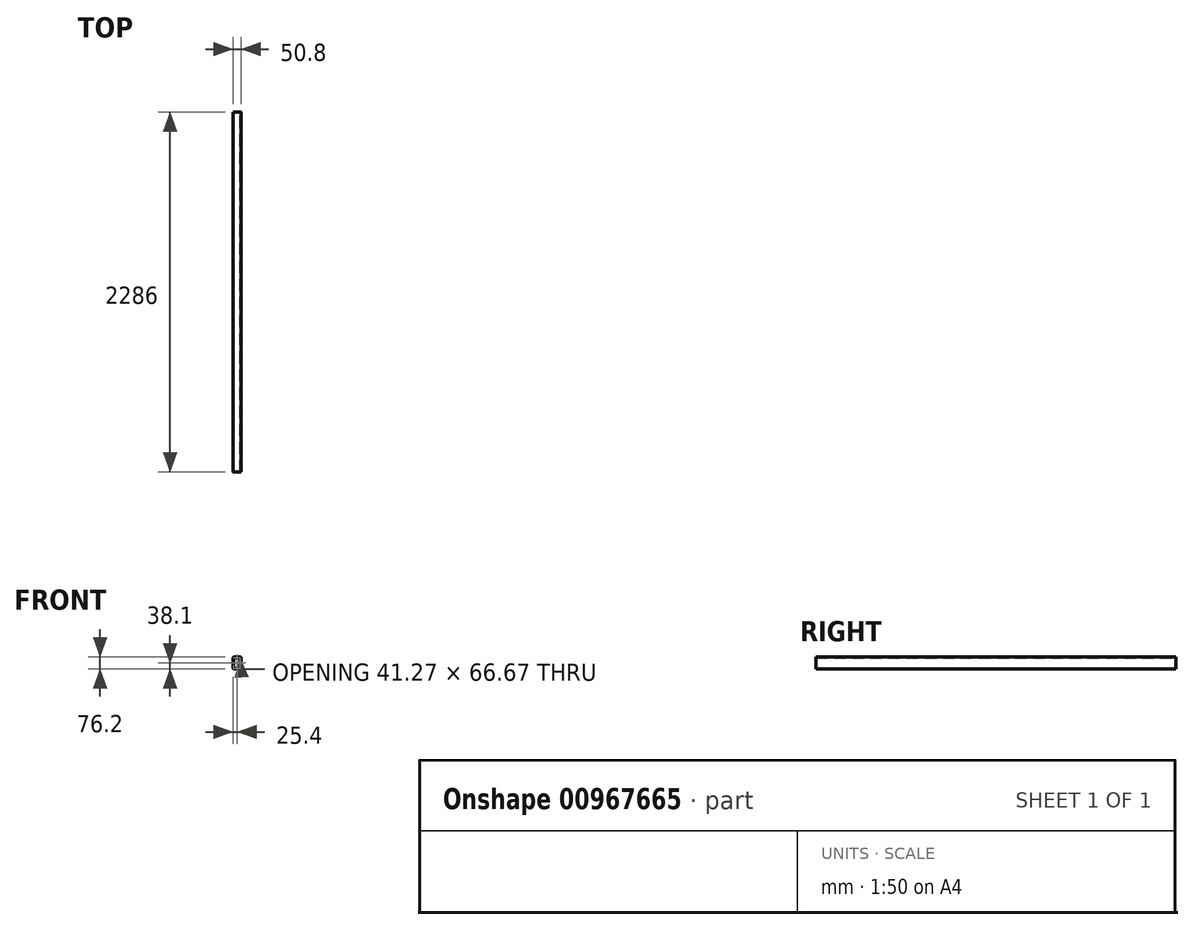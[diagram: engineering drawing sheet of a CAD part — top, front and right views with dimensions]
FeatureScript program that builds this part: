
annotation { "Feature Type Name" : "Feature", "Feature Type Description" : "" }
export const myFeature = defineFeature(function(context is Context, id is Id, definition is map)
    precondition{}
    {
        {
            var Q0;
            Q0=qCreatedBy(makeId("Front.planeOp"),FACE);
            var sketch = newSketch(context, id + "F0", { "sketchPlane" : qUnion([Q0])});
            skLineSegment(sketch, "E0.bottom", {"start": v(6.35, 0) * mm, "end": v(44.45, 0) * mm});
            skLineSegment(sketch, "E0.top", {"start": v(6.35, 76.2) * mm, "end": v(44.45, 76.2) * mm});
            skLineSegment(sketch, "E0.left", {"start": v(0, 6.35) * mm, "end": v(0, 69.85) * mm});
            skLineSegment(sketch, "E0.right", {"start": v(50.8, 6.35) * mm, "end": v(50.8, 69.85) * mm});
            skPoint(sketch, "E1.visualSharp", {"position": v(0, 76.2) * mm});
            skArc(sketch, "E1.filletArc", {"start": v(6.35, 76.2) * mm, "mid": v(1.86, 74.34) * mm, "end": v(0, 69.85) * mm});
            skPoint(sketch, "E2.visualSharp", {"position": v(50.8, 76.2) * mm});
            skArc(sketch, "E2.filletArc", {"start": v(50.8, 69.85) * mm, "mid": v(48.94, 74.34) * mm, "end": v(44.45, 76.2) * mm});
            skPoint(sketch, "E3.visualSharp", {"position": v(50.8, 0) * mm});
            skArc(sketch, "E3.filletArc", {"start": v(44.45, 0) * mm, "mid": v(48.94, 1.86) * mm, "end": v(50.8, 6.35) * mm});
            skPoint(sketch, "E4.visualSharp", {"position": v(0, 0) * mm});
            skArc(sketch, "E4.filletArc", {"start": v(0, 6.35) * mm, "mid": v(1.86, 1.86) * mm, "end": v(6.35, 0) * mm});
            skArc(sketch, "E5.0", {"start": v(6.35, 71.44) * mm, "mid": v(5.23, 70.97) * mm, "end": v(4.76, 69.85) * mm});
            skLineSegment(sketch, "E5.1", {"start": v(4.76, 6.35) * mm, "end": v(4.76, 69.85) * mm});
            skLineSegment(sketch, "E5.2", {"start": v(6.35, 71.44) * mm, "end": v(44.45, 71.44) * mm});
            skArc(sketch, "E5.3", {"start": v(4.76, 6.35) * mm, "mid": v(5.23, 5.23) * mm, "end": v(6.35, 4.76) * mm});
            skArc(sketch, "E5.4", {"start": v(46.04, 69.85) * mm, "mid": v(45.57, 70.97) * mm, "end": v(44.45, 71.44) * mm});
            skLineSegment(sketch, "E5.5", {"start": v(46.04, 6.35) * mm, "end": v(46.04, 69.85) * mm});
            skArc(sketch, "E5.6", {"start": v(44.45, 4.76) * mm, "mid": v(45.57, 5.23) * mm, "end": v(46.04, 6.35) * mm});
            skLineSegment(sketch, "E5.7", {"start": v(6.35, 4.76) * mm, "end": v(44.45, 4.76) * mm});
            skSolve(sketch);
        }
        {
            var Q0;
            Q0 = qSketchRegion(id + "F0", true);
            extrude(context, id + "F1", {"entities" : qUnion([Q0]), "depth" : 2286 * mm, "offsetDistance" : 25.4 * mm});
        }
    });
